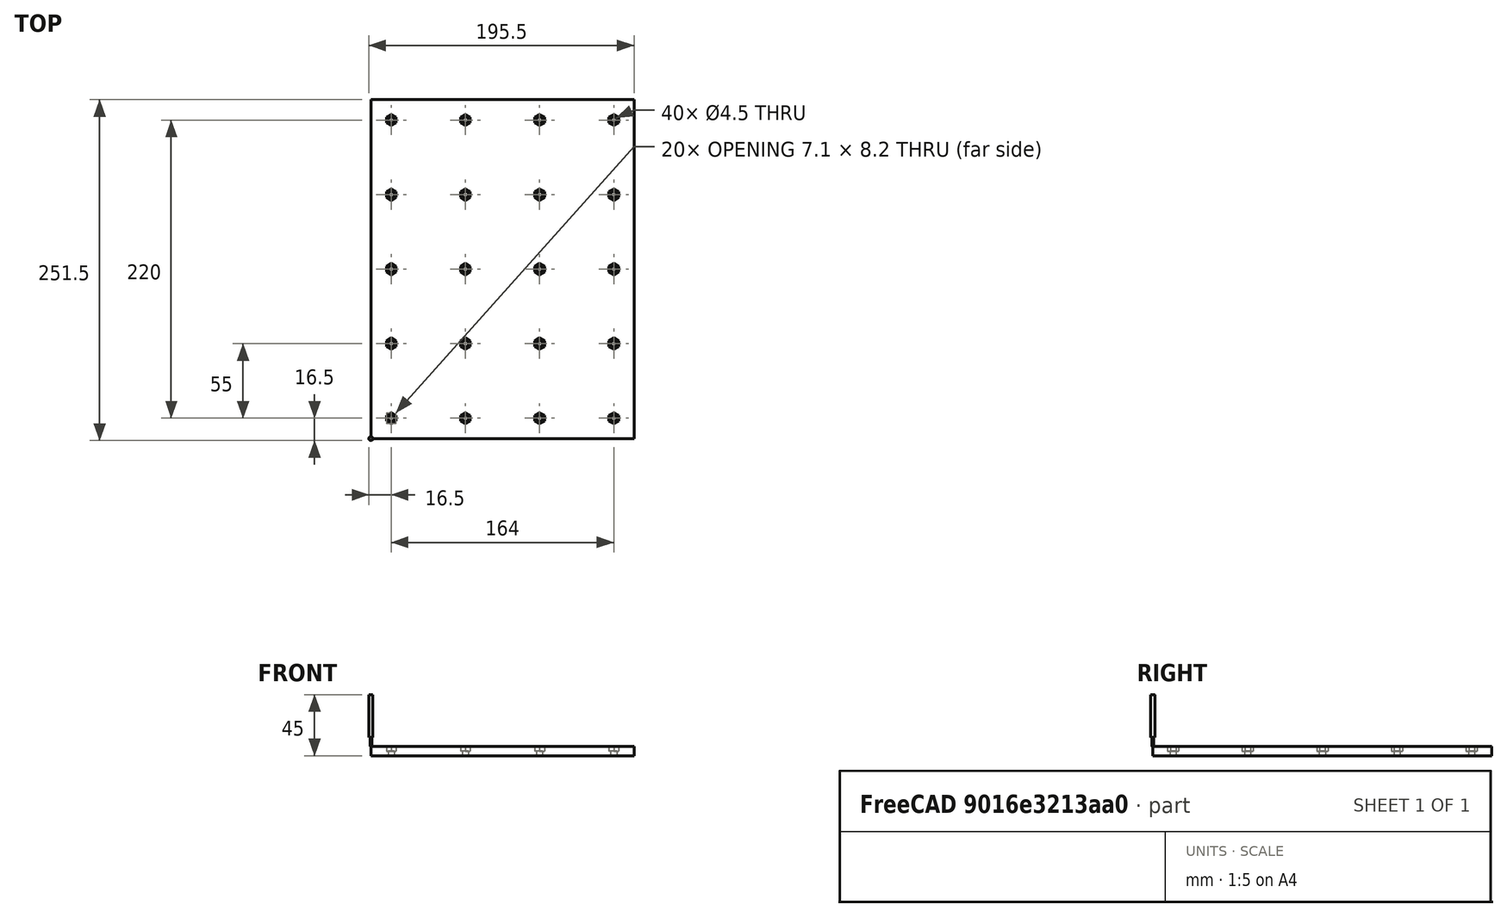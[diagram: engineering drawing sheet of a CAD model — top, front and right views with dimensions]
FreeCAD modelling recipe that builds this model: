
FCSTD DOCUMENT  (FreeCAD 0.20R29410 (Git))
Label: Mesa
License: All rights reserved
LicenseURL: http://en.wikipedia.org/wiki/All_rights_reserved
objects: Sketcher::SketchObject×3, Part::FeaturePython×3, App::DocumentObjectGroup×3, Path::FeaturePython×3, PartDesign::LinearPattern×2, PartDesign::Pad×1, PartDesign::Pocket×1, PartDesign::Hole×1, PartDesign::MultiTransform×1, PartDesign::Body×1, App::FeaturePython×1, Mesh::FeaturePython×1
note: 16 computed .brp shape members not serialized (recipe doc carries the construction recipe); baked Part::Feature solids carry a one-line shape summary decoded from their .brp

FEATURE [Sketcher::SketchObject] Sketch
  FullyConstrained = true
  MapMode = 5
  Support = -> [XY_Plane]
  sketch-geometry (4):
    g0: LineSegment StartX=0 StartY=0 StartZ=0 EndX=194 EndY=0 EndZ=0
    g1: LineSegment StartX=194 StartY=0 StartZ=0 EndX=194 EndY=250 EndZ=0
    g2: LineSegment StartX=194 StartY=250 StartZ=0 EndX=0 EndY=250 EndZ=0
    g3: LineSegment StartX=0 StartY=250 StartZ=0 EndX=0 EndY=0 EndZ=0
  constraints (11):
    c: Coincident(g0,g1)
    c: Coincident(g1,g2)
    c: Coincident(g2,g3)
    c: Coincident(g3,g0)
    c: Horizontal(g0)
    c: Horizontal(g2)
    c: Vertical(g1)
    c: Vertical(g3)
    c: Coincident(g0,g-1)
    c: DistanceX(g2,g2) = 194
    c: DistanceY(g1,g1) = 250
FEATURE [PartDesign::Pad] Pad
  Direction = (0,0,1)
  Length = 7
  Length2 = 10
  Profile = -> Sketch
  ReferenceAxis = -> Sketch [N_Axis]
  Reversed = true
  Type = 0
FEATURE [Sketcher::SketchObject] Sketch001
  FullyConstrained = true
  MapMode = 5
  Support = -> [XY_Plane]
  sketch-geometry (7):
    g0: LineSegment StartX=15 StartY=10.9008 StartZ=0 EndX=18.55 EndY=12.9504 EndZ=0
    g1: LineSegment StartX=18.55 StartY=12.9504 StartZ=0 EndX=18.55 EndY=17.0496 EndZ=0
    g2: LineSegment StartX=18.55 StartY=17.0496 StartZ=0 EndX=15 EndY=19.0992 EndZ=0
    g3: LineSegment StartX=15 StartY=19.0992 StartZ=0 EndX=11.45 EndY=17.0496 EndZ=0
    g4: LineSegment StartX=11.45 StartY=17.0496 StartZ=0 EndX=11.45 EndY=12.9504 EndZ=0
    g5: LineSegment StartX=11.45 StartY=12.9504 StartZ=0 EndX=15 EndY=10.9008 EndZ=0
    g6: Circle CenterX=15 CenterY=15 CenterZ=0 NormalX=0 NormalY=0 NormalZ=1 AngleXU=0 Radius=4.09919
  constraints (17):
    c: Coincident(g0,g1)
    c: Coincident(g1,g2)
    c: Coincident(g2,g3)
    c: Coincident(g3,g4)
    c: Coincident(g4,g5)
    c: Coincident(g5,g0)
    c: Equal(g0, g1-g5) x5
    c: PointOnObject(g0,g6)
    c: PointOnObject(g1,g6)
    c: PointOnObject(g2,g6)
    c: PointOnObject(g3,g6)
    c: PointOnObject(g4,g6)
    c: PointOnObject(g5,g6)
    c: Distance(g6,g-1) = 15
    c: Distance(g6,g-2) = 15
    c: Parallel(g4,g-2)
    c: DistanceX(g3,g1) = 7.1
FEATURE [PartDesign::Pocket] Pocket
  BaseFeature = -> Pad
  Direction = (0,0,-1)
  Length = 3.5
  Length2 = 5
  Profile = -> Sketch001
  ReferenceAxis = -> Sketch001 [N_Axis]
  Type = 0
FEATURE [Sketcher::SketchObject] Sketch002
  FullyConstrained = true
  MapMode = 5
  Support = -> [XY_Plane]
  sketch-geometry (1):
    g0: Circle CenterX=15 CenterY=15 CenterZ=0 NormalX=0 NormalY=0 NormalZ=1 AngleXU=0 Radius=2.25
  constraints (3):
    c: Diameter(g0) = 4.5
    c: Distance(g0,g-1) = 15
    c: Distance(g0,g-2) = 15
FEATURE [PartDesign::Hole] Hole
  BaseFeature = -> Pocket
  CustomThreadClearance = 0
  Depth = 639.371
  DepthType = 1
  Diameter = 4.5
  DrillForDepth = false
  DrillPoint = 1
  DrillPointAngle = 118
  HoleCutCountersinkAngle = 90
  HoleCutCustomValues = false
  HoleCutDepth = 0
  HoleCutDiameter = 6.1
  HoleCutType = 0
  ModelThread = false
  Profile = -> Sketch002
  Tapered = false
  TaperedAngle = 90
  ThreadClass = 0
  ThreadDepth = 639.371
  ThreadDepthType = 0
  ThreadDirection = 0
  ThreadFit = 0
  ThreadSize = 0
  ThreadType = 0
  Threaded = false
  UseCustomThreadClearance = false
FEATURE [PartDesign::LinearPattern] LinearPattern
  Direction = -> Sketch001 [H_Axis]
  Length = 164
  Occurrences = 4
FEATURE [PartDesign::LinearPattern] LinearPattern001
  Direction = -> Sketch001 [V_Axis]
  Length = 220
  Occurrences = 5
FEATURE [PartDesign::MultiTransform] MultiTransform
  BaseFeature = -> Hole
  Originals = -> [Pocket,Hole]
  Transformations = -> [LinearPattern,LinearPattern001]
FEATURE [PartDesign::Body] Body
  Group = -> [Sketch,Pad,Sketch001,Pocket,Sketch002,Hole,MultiTransform,LinearPattern,LinearPattern001]
  Origin = -> Origin
  Tip = -> MultiTransform
FEATURE [App::FeaturePython] SetupSheet  # Path/CAM operation (typed FeaturePython)
  ClearanceHeightExpression = OpStockZMax+SetupSheet.ClearanceHeightOffset
  ClearanceHeightOffset = 5
  CoolantMode = 0
  CoolantModes = None | Flood | Mist
  FinalDepthExpression = OpFinalDepth
  HorizRapid = 25
  SafeHeightExpression = OpStockZMax+SetupSheet.SafeHeightOffset
  SafeHeightOffset = 3
  StartDepthExpression = 0mm
  StepDownExpression = 0.6mm
  VertRapid = 5
FEATURE [Part::FeaturePython] Clone  label="Model-Body"  # Draft clone (typed FeaturePython)
  AttacherType = Attacher::AttachEngine3D
  Fuse = false
  Objects = -> [Body]
  PathResource = Model
  Scale = (1,1,1)
FEATURE [App::DocumentObjectGroup] Model
  Group = -> [Clone]
FEATURE [Part::FeaturePython] Clone001  label="Stock-Body"  # Draft clone (typed FeaturePython)
  AttacherType = Attacher::AttachEngine3D
  Fuse = false
  Objects = -> [Body]
  PathResource = Stock
  Placement = pos=(-1.14e-13,-1.78e-13,2e-15) rot=(0,0,1;0rad)
  Scale = (1,1,1)
  StockType = Unknown
FEATURE [Part::FeaturePython] ToolBit001  label="custom_1.3mm_dremel"  # Path/CAM toolbit (typed FeaturePython)
  BitPropertyNames = Chipload | CuttingEdgeHeight | Diameter | Flutes | Length | Material | ShankDiameter | SpindleDirection
  BitShape = C:/Program Files/FreeCAD 0.20/Mod\Path\Tools\Shape\endmill.fcstd
  Chipload = 0
  CuttingEdgeHeight = 6.65
  Diameter = 1.3
  File = <userpath>/AppData/Roaming/FreeCAD/Macro/Bit/custom_1.3mm_dremel.fctb
  Flutes = 6
  Length = 38
  Material = 0
  ShankDiameter = 3
  ShapeName = endmill
  SpindleDirection = 0
FEATURE [Path::FeaturePython] custom_1_3mm_dremel  label="custom_1.3mm_dremel001"  # Path/CAM operation (typed FeaturePython)
  HorizFeed = 30
  HorizRapid = 25
  SpindleDir = 0
  SpindleSpeed = 1
  Tool = -> ToolBit001
  ToolNumber = 2
  VertFeed = 6.66667
  VertRapid = 5
  expr: HorizRapid = SetupSheet.HorizRapid
  expr: VertRapid = SetupSheet.VertRapid
FEATURE [App::DocumentObjectGroup] Tools
  Group = -> [custom_1_3mm_dremel]
FEATURE [Mesh::FeaturePython] CutMaterial  # WARN: FeaturePython — macro-defined, semantics opaque (R4)
FEATURE [Path::FeaturePython] Helix  # Path/CAM operation (typed FeaturePython)
  Active = true
  Base = -> [Clone]
  ClearanceHeight = 5
  CoolantMode = 0
  CycleTime = 00:03:48
  Direction = 0
  FinalDepth = -5
  OffsetExtra = 0
  OpFinalDepth = -7
  OpStartDepth = 2e-15
  OpStockZMax = 2e-15
  OpStockZMin = -7
  OpToolDiameter = 1.3
  SafeHeight = 3
  StartDepth = -2
  StartRadius = 0
  StartSide = 1
  StepDown = 0.6
  StepOver = 80
  ToolController = -> custom_1_3mm_dremel
  expr: ClearanceHeight = OpStockZMax + SetupSheet.ClearanceHeightOffset
  expr: FinalDepth = -5
  expr: SafeHeight = OpStockZMax + SetupSheet.SafeHeightOffset
  expr: StartDepth = -2
  expr: StepDown = 0.6mm
FEATURE [App::DocumentObjectGroup] Operations
  Group = -> [Helix]
FEATURE [Path::FeaturePython] Job  # Path/CAM operation (typed FeaturePython)
  CycleTime = 00:03:48
  Fixtures = G54
  GeometryTolerance = 0.01
  JobType = 0
  LastPostProcessDate = 2023-07-13 21:03:07.509995
  LastPostProcessOutput = <path> - Copy.nc
  Model = -> Model
  Operations = -> Operations
  OrderOutputBy = 0
  PostProcessor = 8
  PostProcessorOutputFile = <path>
  SetupSheet = -> SetupSheet
  SplitOutput = false
  Stock = -> Clone001
  Tools = -> Tools
note: 2 file-system paths scrubbed to <path> (originals preserved in the JSON sidecar)
